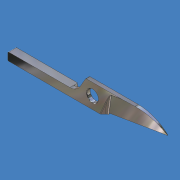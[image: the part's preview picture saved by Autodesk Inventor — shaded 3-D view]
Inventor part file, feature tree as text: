
AUTODESK INVENTOR PART (.ipt)
format: ipt  version: unknown  size: 275,456 bytes
history: native  units: mm (DEFAULTED — no unit token found)
features: sketch x8, fillet x5, extrude x4, plane x3, sweep x1, chamfer x1
ambient origin geometry x8: Origin, YZ Plane, XZ Plane, XY Plane, X Axis, Y Axis, Z Axis, Center Point
feature tree (22):
  extrude  "Extrusion1"  Depth=42.0mm
  fillet  "Fillet1"  Radius=21.5mm
  extrude  "Extrusion2"  Depth=3.0mm
  sketch  "Sketch4"  dims[d6=11.0mm d7=2.0mm d8=20.5mm d9=2.0mm d10=0.0mm d11=120.0deg]
  sketch  "Sketch5"  dims[d12=4.0mm d13=3.0mm]
  plane  "Work Plane3"
  extrude  "Extrusion3"  Depth=2.0mm
  fillet  "Fillet2"  Radius=20.5mm
  fillet  "Fillet4"  Radius=2.0mm
  fillet  "Fillet5"  [1 undecoded]
  plane  "Work Plane4"
  sketch  "Sketch7"  dims[d19=75.0deg]
  plane  "Work Plane5"
  sweep  "Sweep1"
  extrude  "Extrusion4"  Depth=3.0mm
  fillet  "Fillet6"  Radius=15.0mm
  chamfer  "Chamfer1"  Distance=0.1mm
  sketch  "Sketch1"  dims[d0=2.9mm d1=42.0mm d3=21.5mm]
  sketch  "Sketch3"  dims[d4=6.0mm d5=3.0mm]
  sketch  "Sketch6"  dims[d15=2.0mm d16=0.0mm d17=3.0mm d18=15.0mm]
  sketch  "Sketch8"  dims[d20=0.5mm]
  sketch  "Sketch9"  dims[d21=23.5mm d24=0.1mm d25=0.4mm d26=5.0mm d27=15.5mm d28=6.5mm d29=15.5mm d30=2.0mm d31=0.0mm d32=45.0deg d33=0.25mm d35=1.6mm d36=1.0mm d37=0.25mm d38=-0.3mm d39=0.0mm d40=10.0mm d41=0.0mm d42=0.2mm d43=0.1mm d44=0.1mm d45=45.0deg]
note: 1 required parameter value undecoded (feature->parameter linkage not recoverable at this tier; creation-order binding heuristic only, values carry confidence <= 0.55)
